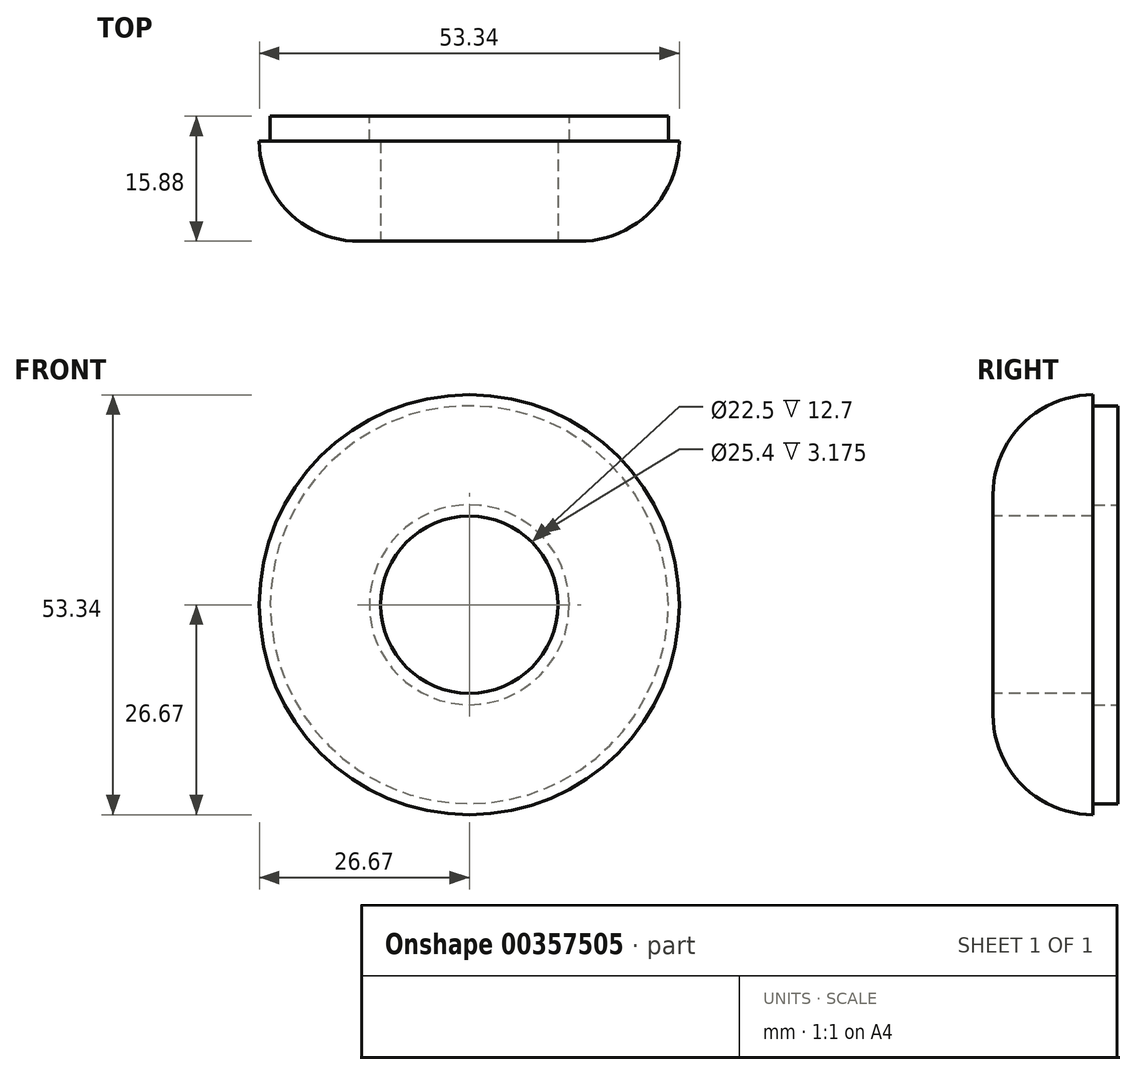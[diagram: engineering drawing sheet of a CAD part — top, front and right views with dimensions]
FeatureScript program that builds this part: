
annotation { "Feature Type Name" : "Feature", "Feature Type Description" : "" }
export const myFeature = defineFeature(function(context is Context, id is Id, definition is map)
    precondition{}
    {
        {
            var Q0;
            Q0=qCreatedBy(makeId("Front.planeOp"),FACE);
            var sketch = newSketch(context, id + "F0", { "sketchPlane" : qUnion([Q0])});
            skCircle(sketch, "E0", {"center": v(0, 0) * mm, "radius": 26.67 * mm});
            skSolve(sketch);
        }
        {
            var Q0;
            Q0=makeQuery(id+"F0.imprint","IMPRINT",FACE,{"disambiguationData":[TD([[makeQuery(id+"F0.imprint","IMPRINT",EDGE,{"derivedFrom":sQuery(id+"F0.wireOp",EDGE,"E0")}),1.0]])]});
            extrude(context, id + "F1", {"entities" : qUnion([Q0]), "depth" : 12.7 * mm});
        }
        {
            var Q0;
            Q0=makeQuery(id+"F1.opExtrude","CAP_FACE",FACE,{"disambiguationData":[OSD([sQuery(id+"F0.wireOp",EDGE,"E0")])],"isStart":false});
            fillet(context, id + "F2", {"entities" : qUnion([Q0]), "radius" : 12.7 * mm, "tangentPropagation" : true, "allowEdgeOverflow" : false});
        }
        {
            var Q0;
            Q0=makeQuery(id+"F1.opExtrude","CAP_FACE",FACE,{"disambiguationData":[OSD([sQuery(id+"F0.wireOp",EDGE,"E0")])],"isStart":false});
            var sketch = newSketch(context, id + "F3", { "sketchPlane" : qUnion([Q0])});
            skCircle(sketch, "E1", {"center": v(0, 0) * mm, "radius": 11.25 * mm});
            skSolve(sketch);
        }
        {
            var Q0;
            Q0=makeQuery(id+"F3.imprint","IMPRINT",FACE,{"disambiguationData":[TD([[makeQuery(id+"F3.imprint","IMPRINT",EDGE,{"derivedFrom":sQuery(id+"F3.wireOp",EDGE,"E1")}),1.0]])]});
            var Q1;
            Q1=sQuery(id+"F3.wireOp",EDGE,"E1");
            extrude(context, id + "F4", {"entities" : qUnion([Q0]), "operationType" : NewBodyOperationType.REMOVE, "surfaceEntities" : qUnion([Q1]), "oppositeDirection" : true, "depth" : 12.7 * mm});
        }
        {
            var Q0;
            Q0=qCreatedBy(makeId("Front.planeOp"),FACE);
            var sketch = newSketch(context, id + "F5", { "sketchPlane" : qUnion([Q0])});
            skCircle(sketch, "E2", {"center": v(0, 0) * mm, "radius": 25.27 * mm});
            skSolve(sketch);
        }
        {
            var Q0;
            Q0 = qSketchRegion(id + "F5", true);
            extrude(context, id + "F6", {"entities" : qUnion([Q0]), "operationType" : NewBodyOperationType.ADD, "depth" : -3.17 * mm});
        }
        {
            var Q0;
            Q0=makeQuery(id+"F6.opExtrude","CAP_FACE",FACE,{"disambiguationData":[OSD([sQuery(id+"F5.wireOp",EDGE,"E2")])],"isStart":false});
            var sketch = newSketch(context, id + "F7", { "sketchPlane" : qUnion([Q0])});
            skCircle(sketch, "E3", {"center": v(0, 0) * mm, "radius": 12.7 * mm});
            skSolve(sketch);
        }
        {
            var Q0;
            Q0=makeQuery(id+"F7.imprint","IMPRINT",FACE,{"disambiguationData":[TD([[makeQuery(id+"F7.imprint","IMPRINT",EDGE,{"derivedFrom":sQuery(id+"F7.wireOp",EDGE,"E3")}),1.0]])]});
            extrude(context, id + "F8", {"entities" : qUnion([Q0]), "operationType" : NewBodyOperationType.REMOVE, "oppositeDirection" : true, "depth" : 3.17 * mm});
        }
    });
